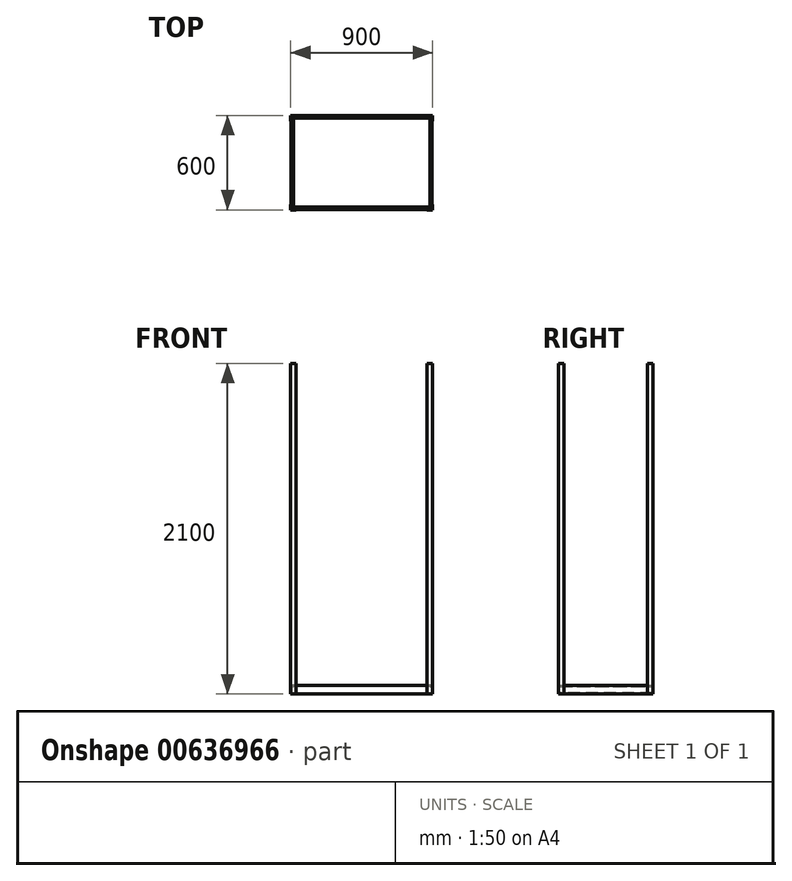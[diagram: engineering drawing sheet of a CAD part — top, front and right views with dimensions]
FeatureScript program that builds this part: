
annotation { "Feature Type Name" : "Feature", "Feature Type Description" : "" }
export const myFeature = defineFeature(function(context is Context, id is Id, definition is map)
    precondition{}
    {
        {
            var Q0;
            Q0=qCreatedBy(makeId("Top.planeOp"),FACE);
            var sketch = newSketch(context, id + "F0", { "sketchPlane" : qUnion([Q0])});
            skLineSegment(sketch, "E0", {"start": v(0, 300) * mm, "end": v(0, -300) * mm, "construction": true});
            skLineSegment(sketch, "E1", {"start": v(450, 0) * mm, "end": v(-450, 0) * mm, "construction": true});
            skLineSegment(sketch, "E2", {"start": v(-450, -300) * mm, "end": v(-450, -265) * mm});
            skLineSegment(sketch, "E3", {"start": v(-450, -265) * mm, "end": v(-448, -265) * mm});
            skLineSegment(sketch, "E4", {"start": v(-448, -265) * mm, "end": v(-448, -298) * mm});
            skLineSegment(sketch, "E5", {"start": v(-448, -298) * mm, "end": v(-415, -298) * mm});
            skLineSegment(sketch, "E6", {"start": v(-415, -298) * mm, "end": v(-415, -300) * mm});
            skLineSegment(sketch, "E7", {"start": v(-415, -300) * mm, "end": v(-450, -300) * mm});
            skLineSegment(sketch, "E8.MirrorCS", {"start": v(450, -265) * mm, "end": v(448, -265) * mm});
            skLineSegment(sketch, "E9.MirrorCS", {"start": v(415, -298) * mm, "end": v(415, -300) * mm});
            skLineSegment(sketch, "E10.MirrorCS", {"start": v(448, -298) * mm, "end": v(415, -298) * mm});
            skLineSegment(sketch, "E11.MirrorCS", {"start": v(448, -265) * mm, "end": v(448, -298) * mm});
            skLineSegment(sketch, "E12.MirrorCS", {"start": v(415, -300) * mm, "end": v(450, -300) * mm});
            skLineSegment(sketch, "E13.MirrorCS", {"start": v(450, -300) * mm, "end": v(450, -265) * mm});
            skLineSegment(sketch, "E14.MirrorCS", {"start": v(450, 265) * mm, "end": v(448, 265) * mm});
            skLineSegment(sketch, "E15.MirrorCS", {"start": v(415, 298) * mm, "end": v(415, 300) * mm});
            skLineSegment(sketch, "E16.MirrorCS", {"start": v(415, 300) * mm, "end": v(450, 300) * mm});
            skLineSegment(sketch, "E17.MirrorCS", {"start": v(450, 300) * mm, "end": v(450, 265) * mm});
            skLineSegment(sketch, "E18.MirrorCS", {"start": v(448, 298) * mm, "end": v(415, 298) * mm});
            skLineSegment(sketch, "E19.MirrorCS", {"start": v(448, 265) * mm, "end": v(448, 298) * mm});
            skLineSegment(sketch, "E20.MirrorCS", {"start": v(-415, 298) * mm, "end": v(-415, 300) * mm});
            skLineSegment(sketch, "E21.MirrorCS", {"start": v(-450, 300) * mm, "end": v(-450, 265) * mm});
            skLineSegment(sketch, "E22.MirrorCS", {"start": v(-448, 298) * mm, "end": v(-415, 298) * mm});
            skLineSegment(sketch, "E23.MirrorCS", {"start": v(-450, 265) * mm, "end": v(-448, 265) * mm});
            skLineSegment(sketch, "E24.MirrorCS", {"start": v(-415, 300) * mm, "end": v(-450, 300) * mm});
            skLineSegment(sketch, "E25.MirrorCS", {"start": v(-448, 265) * mm, "end": v(-448, 298) * mm});
            skSolve(sketch);
        }
        {
            var Q0;
            Q0=qCreatedBy(makeId("Top.planeOp"),FACE);
            var sketch = newSketch(context, id + "F1", { "sketchPlane" : qUnion([Q0])});
            skLineSegment(sketch, "E26", {"start": v(-446, 0) * mm, "end": v(446, 0) * mm, "construction": true});
            skLineSegment(sketch, "E27", {"start": v(0, -296) * mm, "end": v(0, 296) * mm, "construction": true});
            skLineSegment(sketch, "E28.bottom", {"start": v(-446, 296) * mm, "end": v(446, 296) * mm});
            skLineSegment(sketch, "E28.top", {"start": v(-446, -296) * mm, "end": v(446, -296) * mm});
            skLineSegment(sketch, "E28.left", {"start": v(-446, 296) * mm, "end": v(-446, -296) * mm});
            skLineSegment(sketch, "E28.right", {"start": v(446, 296) * mm, "end": v(446, -296) * mm});
            skPoint(sketch, "E28.middle", {"position": v(0, 0) * mm});
            skSolve(sketch);
        }
        {
            var Q0;
            Q0=makeQuery(id+"F1.imprint","IMPRINT",FACE,{"disambiguationData":[TD([[makeQuery(id+"F1.imprint","IMPRINT",EDGE,{"derivedFrom":sQuery(id+"F1.wireOp",EDGE,"E28.bottom")}),-1.0]])]});
            extrude(context, id + "F2", {"entities" : qUnion([Q0]), "depth" : 7 * mm, "offsetDistance" : 25 * mm});
        }
        {
            var Q0;
            Q0=makeQuery(id+"F0.imprint","IMPRINT",FACE,{"disambiguationData":[TD([[makeQuery(id+"F0.imprint","IMPRINT",EDGE,{"derivedFrom":sQuery(id+"F0.wireOp",EDGE,"E2")}),-1.0]])]});
            var Q1;
            Q1=makeQuery(id+"F0.imprint","IMPRINT",FACE,{"disambiguationData":[TD([[makeQuery(id+"F0.imprint","IMPRINT",EDGE,{"derivedFrom":sQuery(id+"F0.wireOp",EDGE,"E8.MirrorCS")}),1.0]])]});
            var Q2;
            Q2=makeQuery(id+"F0.imprint","IMPRINT",FACE,{"disambiguationData":[TD([[makeQuery(id+"F0.imprint","IMPRINT",EDGE,{"derivedFrom":sQuery(id+"F0.wireOp",EDGE,"E14.MirrorCS")}),-1.0]])]});
            var Q3;
            Q3=makeQuery(id+"F0.imprint","IMPRINT",FACE,{"disambiguationData":[TD([[makeQuery(id+"F0.imprint","IMPRINT",EDGE,{"derivedFrom":sQuery(id+"F0.wireOp",EDGE,"E20.MirrorCS")}),1.0]])]});
            extrude(context, id + "F3", {"entities" : qUnion([Q0, Q1, Q2, Q3]), "depth" : 2100 * mm, "offsetDistance" : 25 * mm});
        }
        {
            var Q0;
            Q0=qCreatedBy(makeId("Right.planeOp"),FACE);
            var sketch = newSketch(context, id + "F4", { "sketchPlane" : qUnion([Q0])});
            skLineSegment(sketch, "E29", {"start": v(0, 109.63) * mm, "end": v(0, -109.63) * mm, "construction": true});
            skLineSegment(sketch, "E30", {"start": v(-298, 0) * mm, "end": v(298, 0) * mm, "construction": true});
            skLineSegment(sketch, "E31", {"start": v(-298, 0) * mm, "end": v(-298, 56) * mm});
            skLineSegment(sketch, "E32", {"start": v(-298, 56) * mm, "end": v(-296, 56) * mm});
            skLineSegment(sketch, "E33", {"start": v(-296, 56) * mm, "end": v(-296, 49) * mm});
            skLineSegment(sketch, "E34", {"start": v(-296, 49) * mm, "end": v(-283, 49) * mm});
            skLineSegment(sketch, "E35", {"start": v(-283, 49) * mm, "end": v(-283, 47) * mm});
            skLineSegment(sketch, "E36", {"start": v(-283, 47) * mm, "end": v(-296, 47) * mm});
            skLineSegment(sketch, "E37", {"start": v(-296, 47) * mm, "end": v(-296, 2) * mm});
            skLineSegment(sketch, "E38", {"start": v(-296, 2) * mm, "end": v(-283, 2) * mm});
            skLineSegment(sketch, "E39", {"start": v(-283, 2) * mm, "end": v(-283, 0) * mm});
            skLineSegment(sketch, "E40", {"start": v(-283, 0) * mm, "end": v(-298, 0) * mm});
            skLineSegment(sketch, "E41.MirrorCS", {"start": v(296, 56) * mm, "end": v(296, 49) * mm});
            skLineSegment(sketch, "E42.MirrorCS", {"start": v(298, 56) * mm, "end": v(296, 56) * mm});
            skLineSegment(sketch, "E43.MirrorCS", {"start": v(283, 2) * mm, "end": v(283, 0) * mm});
            skLineSegment(sketch, "E44.MirrorCS", {"start": v(283, 49) * mm, "end": v(283, 47) * mm});
            skLineSegment(sketch, "E45.MirrorCS", {"start": v(296, 2) * mm, "end": v(283, 2) * mm});
            skLineSegment(sketch, "E46.MirrorCS", {"start": v(296, 49) * mm, "end": v(283, 49) * mm});
            skLineSegment(sketch, "E47.MirrorCS", {"start": v(283, 47) * mm, "end": v(296, 47) * mm});
            skLineSegment(sketch, "E48.MirrorCS", {"start": v(283, 0) * mm, "end": v(298, 0) * mm});
            skLineSegment(sketch, "E49.MirrorCS", {"start": v(296, 47) * mm, "end": v(296, 2) * mm});
            skLineSegment(sketch, "E50.MirrorCS", {"start": v(298, 0) * mm, "end": v(298, 56) * mm});
            skLineSegment(sketch, "E51.MirrorCS", {"start": v(298, 0) * mm, "end": v(-298, 0) * mm, "construction": true});
            skSolve(sketch);
        }
        {
            var Q0;
            Q0=makeQuery(id+"F4.imprint","IMPRINT",FACE,{"disambiguationData":[TD([[makeQuery(id+"F4.imprint","IMPRINT",EDGE,{"derivedFrom":sQuery(id+"F4.wireOp",EDGE,"E31")}),-1.0]])]});
            var Q1;
            Q1=makeQuery(id+"F4.imprint","IMPRINT",FACE,{"disambiguationData":[TD([[makeQuery(id+"F4.imprint","IMPRINT",EDGE,{"derivedFrom":sQuery(id+"F4.wireOp",EDGE,"E41.MirrorCS")}),1.0]])]});
            extrude(context, id + "F5", {"entities" : qUnion([Q0, Q1]), "endBound" : BoundingType.SYMMETRIC, "depth" : 896 * mm, "offsetDistance" : 25 * mm, "hasSecondDirection" : true, "secondDirectionOppositeDirection" : true, "secondDirectionDepth" : 25 * mm});
        }
        {
            var Q0;
            Q0=makeQuery(id+"F5.opExtrude","CAP_EDGE",EDGE,{"disambiguationData":[OSD([sQuery(id+"F4.wireOp",EDGE,"E44.MirrorCS")])],"isStart":true});
            var Q1;
            Q1=makeQuery(id+"F5.opExtrude","CAP_EDGE",EDGE,{"disambiguationData":[OSD([sQuery(id+"F4.wireOp",EDGE,"E43.MirrorCS")])],"isStart":true});
            var Q2;
            Q2=makeQuery(id+"F5.opExtrude","CAP_EDGE",EDGE,{"disambiguationData":[OSD([sQuery(id+"F4.wireOp",EDGE,"E44.MirrorCS")])],"isStart":false});
            var Q3;
            Q3=makeQuery(id+"F5.opExtrude","CAP_EDGE",EDGE,{"disambiguationData":[OSD([sQuery(id+"F4.wireOp",EDGE,"E43.MirrorCS")])],"isStart":false});
            var Q4;
            Q4=makeQuery(id+"F5.opExtrude","CAP_EDGE",EDGE,{"disambiguationData":[OSD([sQuery(id+"F4.wireOp",EDGE,"E35")])],"isStart":false});
            var Q5;
            Q5=makeQuery(id+"F5.opExtrude","CAP_EDGE",EDGE,{"disambiguationData":[OSD([sQuery(id+"F4.wireOp",EDGE,"E39")])],"isStart":false});
            var Q6;
            Q6=makeQuery(id+"F5.opExtrude","CAP_EDGE",EDGE,{"disambiguationData":[OSD([sQuery(id+"F4.wireOp",EDGE,"E35")])],"isStart":true});
            var Q7;
            Q7=makeQuery(id+"F5.opExtrude","CAP_EDGE",EDGE,{"disambiguationData":[OSD([sQuery(id+"F4.wireOp",EDGE,"E39")])],"isStart":true});
            chamfer(context, id + "F6", {"entities" : qUnion([Q0, Q1, Q2, Q3, Q4, Q5, Q6, Q7]), "chamferType" : ChamferType.OFFSET_ANGLE, "width" : 13 * mm, "oppositeDirection" : false, "angle" : 45 * degree, "tangentPropagation" : true});
        }
        {
            var Q0;
            Q0=qCreatedBy(makeId("Front.planeOp"),FACE);
            var sketch = newSketch(context, id + "F7", { "sketchPlane" : qUnion([Q0])});
            skLineSegment(sketch, "E52", {"start": v(448, 0) * mm, "end": v(-448, 0) * mm, "construction": true});
            skLineSegment(sketch, "E53", {"start": v(0, 105.73) * mm, "end": v(0, -105.73) * mm, "construction": true});
            skLineSegment(sketch, "E54", {"start": v(-448, 0) * mm, "end": v(-448, 56) * mm});
            skLineSegment(sketch, "E55", {"start": v(-448, 56) * mm, "end": v(-446, 56) * mm});
            skLineSegment(sketch, "E56", {"start": v(-446, 56) * mm, "end": v(-446, 49) * mm});
            skLineSegment(sketch, "E57", {"start": v(-446, 49) * mm, "end": v(-433, 49) * mm});
            skLineSegment(sketch, "E58", {"start": v(-433, 49) * mm, "end": v(-433, 47) * mm});
            skLineSegment(sketch, "E59", {"start": v(-433, 47) * mm, "end": v(-446, 47) * mm});
            skLineSegment(sketch, "E60", {"start": v(-446, 47) * mm, "end": v(-446, 2) * mm});
            skLineSegment(sketch, "E61", {"start": v(-446, 2) * mm, "end": v(-433, 2) * mm});
            skLineSegment(sketch, "E62", {"start": v(-433, 2) * mm, "end": v(-433, 0) * mm});
            skLineSegment(sketch, "E63", {"start": v(-433, 0) * mm, "end": v(-448, 0) * mm});
            skLineSegment(sketch, "E64.MirrorCS", {"start": v(433, 2) * mm, "end": v(433, 0) * mm});
            skLineSegment(sketch, "E65.MirrorCS", {"start": v(433, 49) * mm, "end": v(433, 47) * mm});
            skLineSegment(sketch, "E66.MirrorCS", {"start": v(448, 56) * mm, "end": v(446, 56) * mm});
            skLineSegment(sketch, "E67.MirrorCS", {"start": v(446, 56) * mm, "end": v(446, 49) * mm});
            skLineSegment(sketch, "E68.MirrorCS", {"start": v(433, 0) * mm, "end": v(448, 0) * mm});
            skLineSegment(sketch, "E69.MirrorCS", {"start": v(448, 0) * mm, "end": v(448, 56) * mm});
            skLineSegment(sketch, "E70.MirrorCS", {"start": v(446, 2) * mm, "end": v(433, 2) * mm});
            skLineSegment(sketch, "E71.MirrorCS", {"start": v(446, 47) * mm, "end": v(446, 2) * mm});
            skLineSegment(sketch, "E72.MirrorCS", {"start": v(446, 49) * mm, "end": v(433, 49) * mm});
            skLineSegment(sketch, "E73.MirrorCS", {"start": v(433, 47) * mm, "end": v(446, 47) * mm});
            skSolve(sketch);
        }
        {
            var Q0;
            Q0=makeQuery(id+"F7.imprint","IMPRINT",FACE,{"disambiguationData":[TD([[makeQuery(id+"F7.imprint","IMPRINT",EDGE,{"derivedFrom":sQuery(id+"F7.wireOp",EDGE,"E54")}),-1.0]])]});
            var Q1;
            Q1=makeQuery(id+"F7.imprint","IMPRINT",FACE,{"disambiguationData":[TD([[makeQuery(id+"F7.imprint","IMPRINT",EDGE,{"derivedFrom":sQuery(id+"F7.wireOp",EDGE,"E64.MirrorCS")}),1.0]])]});
            extrude(context, id + "F8", {"entities" : qUnion([Q0, Q1]), "endBound" : BoundingType.SYMMETRIC, "depth" : 596 * mm, "offsetDistance" : 25 * mm});
        }
        {
            var Q0;
            Q0=makeQuery(id+"F8.opExtrude","CAP_EDGE",EDGE,{"disambiguationData":[OSD([sQuery(id+"F7.wireOp",EDGE,"E65.MirrorCS")])],"isStart":true});
            var Q1;
            Q1=makeQuery(id+"F8.opExtrude","CAP_EDGE",EDGE,{"disambiguationData":[OSD([sQuery(id+"F7.wireOp",EDGE,"E64.MirrorCS")])],"isStart":true});
            var Q2;
            Q2=makeQuery(id+"F8.opExtrude","CAP_EDGE",EDGE,{"disambiguationData":[OSD([sQuery(id+"F7.wireOp",EDGE,"E64.MirrorCS")])],"isStart":false});
            var Q3;
            Q3=makeQuery(id+"F8.opExtrude","CAP_EDGE",EDGE,{"disambiguationData":[OSD([sQuery(id+"F7.wireOp",EDGE,"E65.MirrorCS")])],"isStart":false});
            var Q4;
            Q4=makeQuery(id+"F8.opExtrude","CAP_EDGE",EDGE,{"disambiguationData":[OSD([sQuery(id+"F7.wireOp",EDGE,"E58")])],"isStart":false});
            var Q5;
            Q5=makeQuery(id+"F8.opExtrude","CAP_EDGE",EDGE,{"disambiguationData":[OSD([sQuery(id+"F7.wireOp",EDGE,"E62")])],"isStart":false});
            var Q6;
            Q6=makeQuery(id+"F8.opExtrude","CAP_EDGE",EDGE,{"disambiguationData":[OSD([sQuery(id+"F7.wireOp",EDGE,"E58")])],"isStart":true});
            var Q7;
            Q7=makeQuery(id+"F8.opExtrude","CAP_EDGE",EDGE,{"disambiguationData":[OSD([sQuery(id+"F7.wireOp",EDGE,"E62")])],"isStart":true});
            chamfer(context, id + "F9", {"entities" : qUnion([Q0, Q1, Q2, Q3, Q4, Q5, Q6, Q7]), "chamferType" : ChamferType.OFFSET_ANGLE, "width" : 13 * mm, "oppositeDirection" : false, "angle" : 45 * degree, "tangentPropagation" : true});
        }
    });
